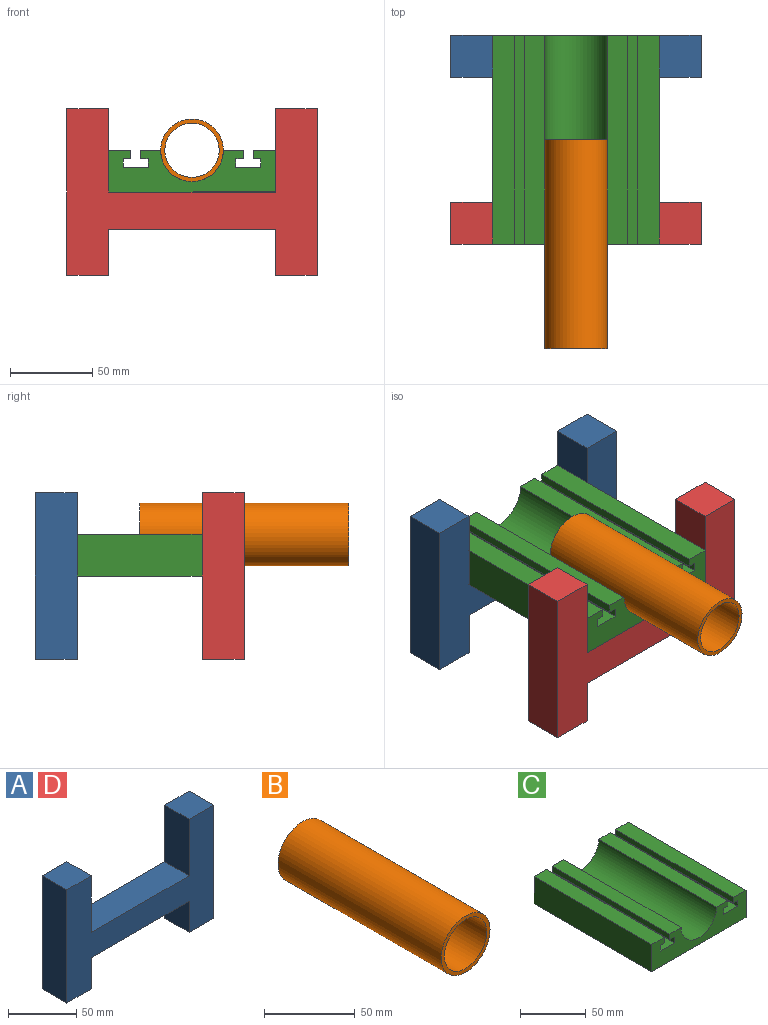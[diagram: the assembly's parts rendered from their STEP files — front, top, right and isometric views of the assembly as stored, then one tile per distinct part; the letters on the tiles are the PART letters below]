
ASSEMBLY  parts=4 mates=7
PART A: 14 faces, bbox 152.4x25.4x101.6 mm
  f0: plane 25.4x25.4mm, normal (0,0,1), area 645.2mm2, adj f1,f11,f12,f13
  f1: plane 50.8x25.4mm, normal (-1,0,0), area 1290.3mm2, adj f0,f2,f12,f13
  f2: plane 101.6x25.4mm, normal (0,0,1), area 2580.6mm2, adj f1,f3,f12,f13
  f3: plane 50.8x25.4mm, normal (1,0,0), area 1290.3mm2, adj f2,f4,f12,f13
  f4: plane 25.4x25.4mm, normal (0,0,1), area 645.2mm2, adj f3,f5,f12,f13
  f5: plane 101.6x25.4mm, normal (-1,0,0), area 2580.6mm2, adj f4,f6,f12,f13
  f6: plane 25.4x25.4mm, normal (0,0,-1), area 645.2mm2, adj f5,f7,f12,f13
  f7: plane 28.03x25.4mm, normal (1,0,0), area 712.1mm2, adj f6,f8,f12,f13
  f8: plane 101.6x25.4mm, normal (0,0,-1), area 2580.6mm2, adj f7,f9,f12,f13
  f9: plane 28.03x25.4mm, normal (-1,0,0), area 712.1mm2, adj f8,f10,f12,f13
  f10: plane 25.4x25.4mm, normal (0,0,-1), area 645.2mm2, adj f9,f11,f12,f13
  f11: plane 101.6x25.4mm, normal (1,0,0), area 2580.6mm2, adj f0,f10,f12,f13
  f12: plane 152.4x101.6mm, normal (0,-1,0), area 7474.3mm2, adj f0,f1,f2,f3,f4,f5,f6,f7
  f13: plane 152.4x101.6mm, normal (0,1,0), area 7474.3mm2, adj f0,f1,f2,f3,f4,f5,f6,f7
PART B: 4 faces, bbox 38.1x127x38.1 mm
  f0: cylinder r=19.05mm len=127mm, axis (0,1,0), area 15201.2mm2, adj f1,f2
  f1: plane 38.1x38.1mm, normal (0,-1,0), area 284.5mm2, adj f0,f3
  f2: plane 38.1x38.1mm, normal (0,1,0), area 284.5mm2, adj f0,f3
  f3: cylinder r=16.5mm len=127mm, axis (0,-1,0), area 13168.3mm2, adj f1,f2
PART C: 24 faces, bbox 101.6x127x25.4 mm
  f0: plane 127x25.4mm, normal (1,0,0), area 3225.8mm2, adj f1,f21,f22,f23
  f1: plane 127x13.59mm, normal (0,0,1), area 1725.8mm2, adj f0,f2,f22,f23
  f2: plane 127x5.08mm, normal (-1,0,0), area 645.2mm2, adj f1,f3,f22,f23
  f3: plane 127x4.7mm, normal (0,0,-1), area 596.8mm2, adj f2,f4,f22,f23
  f4: plane 127x5.46mm, normal (-1,0,0), area 693.5mm2, adj f3,f5,f22,f23
  f5: plane 127x15.24mm, normal (0,0,1), area 1935.5mm2, adj f4,f6,f22,f23
  f6: plane 127x5.46mm, normal (1,0,0), area 693.5mm2, adj f5,f7,f22,f23
  f7: plane 127x4.7mm, normal (0,0,-1), area 596.8mm2, adj f6,f8,f22,f23
  f8: plane 127x5.08mm, normal (1,0,0), area 645.2mm2, adj f7,f9,f22,f23
  f9: plane 127x12.32mm, normal (0,0,1), area 1564.5mm2, adj f8,f10,f22,f23
  f10: cylinder r=19.05mm len=127mm, axis (0,-1,0), area 7600.6mm2, adj f9,f11,f22,f23
  f11: plane 127x12.32mm, normal (0,0,1), area 1564.5mm2, adj f10,f12,f22,f23
  f12: plane 127x5.08mm, normal (-1,0,0), area 645.2mm2, adj f11,f13,f22,f23
  f13: plane 127x4.7mm, normal (0,0,-1), area 596.8mm2, adj f12,f14,f22,f23
  f14: plane 127x5.46mm, normal (-1,0,0), area 693.5mm2, adj f13,f15,f22,f23
  f15: plane 127x15.24mm, normal (0,0,1), area 1935.5mm2, adj f14,f16,f22,f23
  f16: plane 127x5.46mm, normal (1,0,0), area 693.5mm2, adj f15,f17,f22,f23
  f17: plane 127x4.7mm, normal (0,0,-1), area 596.8mm2, adj f16,f18,f22,f23
  f18: plane 127x5.08mm, normal (1,0,0), area 645.2mm2, adj f17,f19,f22,f23
  f19: plane 127x13.59mm, normal (0,0,1), area 1725.8mm2, adj f18,f20,f22,f23
  f20: plane 127x25.4mm, normal (-1,0,0), area 3225.8mm2, adj f19,f21,f22,f23
  f21: plane 127x101.6mm, normal (0,0,-1), area 12903.2mm2, adj f0,f20,f22,f23
  f22: plane 101.6x25.4mm, normal (0,1,0), area 1784.8mm2, adj f0,f1,f2,f3,f4,f5,f6,f7
  f23: plane 101.6x25.4mm, normal (0,-1,0), area 1784.8mm2, adj f0,f1,f2,f3,f4,f5,f6,f7
PART D: same geometry as A
PLACE A t=(-10.68,59.6,3.4)mm
PLACE B t=(-10.68,-3.9,28.8)mm
PLACE C t=(-10.68,-67.4,16.1)mm
PLACE D t=(-10.68,-42,3.4)mm
MATE planar D.f12 <-> C.f23  axis (0,-1,0) through (65.52,-67.4,3.4)mm
MATE planar A.f3 <-> C.f20  axis (1,0,0) through (-61.48,59.6,28.8)mm
MATE planar B.f0 <-> C.f10  axis (0,1,0) through (-10.68,-67.4,28.8)mm
MATE planar A.f13 <-> C.f22  axis (0,1,0) through (40.12,59.6,-19.37)mm
MATE planar D.f3 <-> C.f20  axis (1,0,0) through (-61.48,-54.7,28.8)mm
MATE planar C.f21 <-> A.f2  axis (0,0,-1) through (-10.68,-3.9,3.4)mm
MATE planar D.f2 <-> C.f21  axis (0,0,1) through (-10.68,-54.7,3.4)mm
